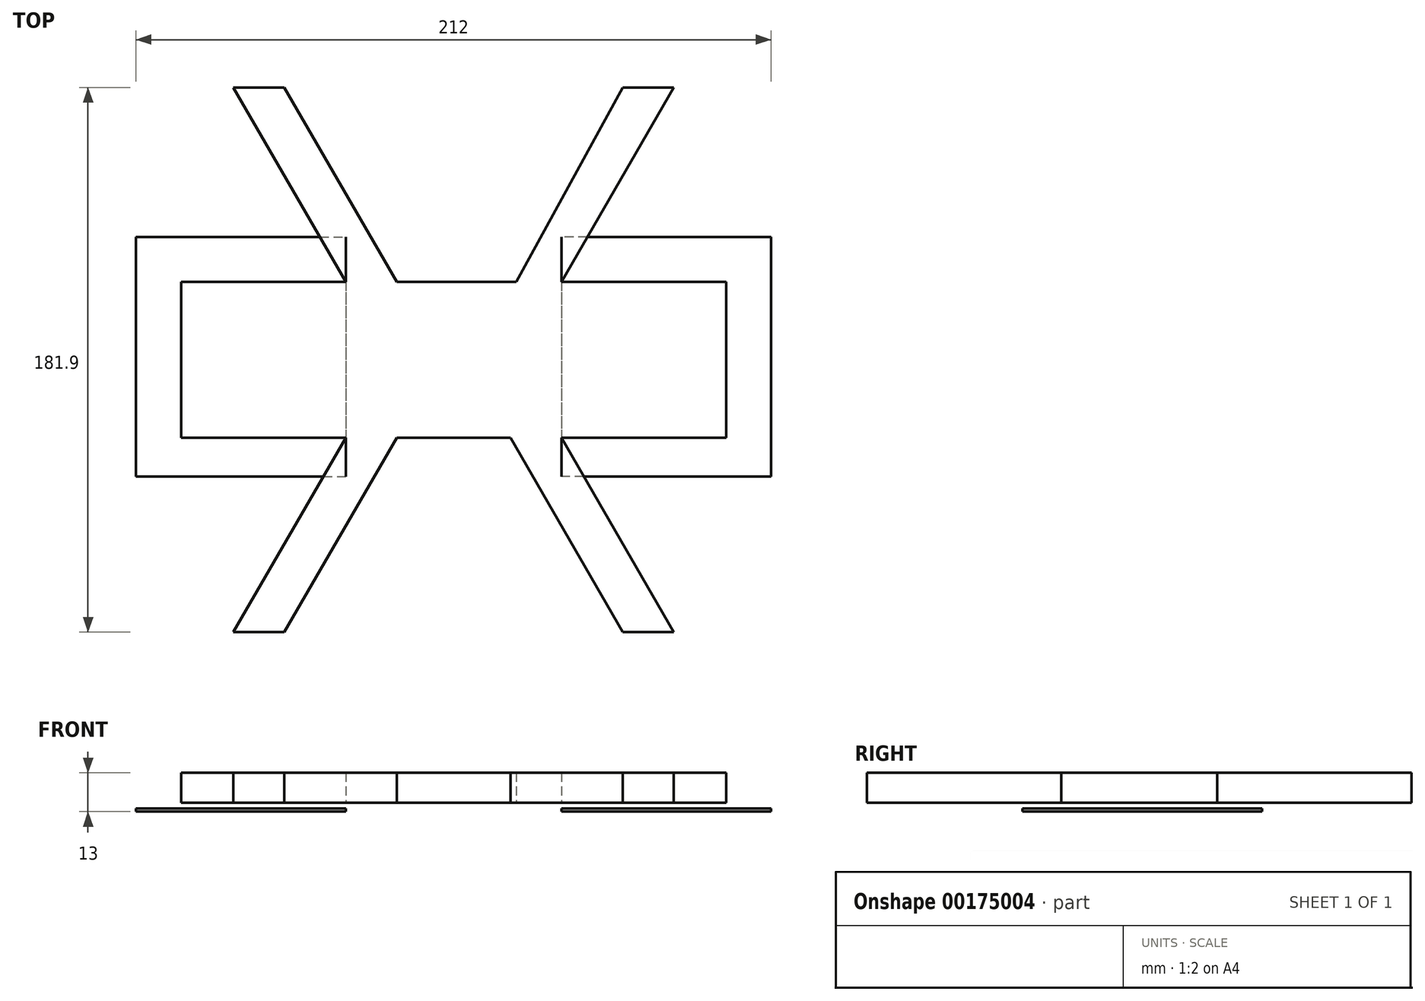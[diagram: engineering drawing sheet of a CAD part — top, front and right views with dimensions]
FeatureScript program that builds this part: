
annotation { "Feature Type Name" : "Feature", "Feature Type Description" : "" }
export const myFeature = defineFeature(function(context is Context, id is Id, definition is map)
    precondition{}
    {
        {
            var Q0;
            Q0=qCreatedBy(makeId("Top.planeOp"),FACE);
            var sketch = newSketch(context, id + "F0", { "sketchPlane" : qUnion([Q0])});
            skLineSegment(sketch, "E0.bottom", {"start": v(0, 0) * mm, "end": v(182, 0) * mm});
            skLineSegment(sketch, "E0.top", {"start": v(0, -52) * mm, "end": v(182, -52) * mm});
            skLineSegment(sketch, "E0.left", {"start": v(0, 0) * mm, "end": v(0, -52) * mm});
            skLineSegment(sketch, "E0.right", {"start": v(182, 0) * mm, "end": v(182, -52) * mm});
            skLineSegment(sketch, "E1", {"start": v(55, 0) * mm, "end": v(17.5, 64.95) * mm});
            skLineSegment(sketch, "E2", {"start": v(17.5, 64.95) * mm, "end": v(34.5, 64.95) * mm});
            skLineSegment(sketch, "E3", {"start": v(34.5, 64.95) * mm, "end": v(72, 0) * mm});
            skLineSegment(sketch, "E4", {"start": v(72, 0) * mm, "end": v(55, 0) * mm});
            skLineSegment(sketch, "E5", {"start": v(112, 0) * mm, "end": v(147.5, 64.95) * mm});
            skLineSegment(sketch, "E6", {"start": v(147.5, 64.95) * mm, "end": v(164.5, 64.95) * mm});
            skLineSegment(sketch, "E7", {"start": v(164.5, 64.95) * mm, "end": v(127, 0) * mm});
            skLineSegment(sketch, "E8", {"start": v(127, 0) * mm, "end": v(112, 0) * mm});
            skLineSegment(sketch, "E9", {"start": v(55, -52) * mm, "end": v(17.5, -116.95) * mm});
            skLineSegment(sketch, "E10", {"start": v(17.5, -116.95) * mm, "end": v(34.5, -116.95) * mm});
            skLineSegment(sketch, "E11", {"start": v(34.5, -116.95) * mm, "end": v(72, -52) * mm});
            skLineSegment(sketch, "E12", {"start": v(72, -52) * mm, "end": v(55, -52) * mm});
            skLineSegment(sketch, "E13", {"start": v(127, -52) * mm, "end": v(164.5, -116.95) * mm});
            skLineSegment(sketch, "E14", {"start": v(164.5, -116.95) * mm, "end": v(147.5, -116.95) * mm});
            skLineSegment(sketch, "E15", {"start": v(147.5, -116.95) * mm, "end": v(110, -52) * mm});
            skLineSegment(sketch, "E16", {"start": v(110, -52) * mm, "end": v(127, -52) * mm});
            skLineSegment(sketch, "E17", {"start": v(55, -52) * mm, "end": v(72, -52) * mm});
            skSolve(sketch);
        }
        {
            var Q0;
            Q0 = qSketchRegion(id + "F0", true);
            extrude(context, id + "F1", {"entities" : qUnion([Q0]), "depth" : 10 * mm});
        }
        {
            var Q0;
            Q0=qCreatedBy(makeId("Top.planeOp"),FACE);
            var sketch = newSketch(context, id + "F2", { "sketchPlane" : qUnion([Q0])});
            skLineSegment(sketch, "E18.bottom", {"start": v(-15, 15) * mm, "end": v(55, 15) * mm});
            skLineSegment(sketch, "E18.top", {"start": v(-15, -65) * mm, "end": v(55, -65) * mm});
            skLineSegment(sketch, "E18.left", {"start": v(-15, 15) * mm, "end": v(-15, -65) * mm});
            skLineSegment(sketch, "E18.right", {"start": v(55, 15) * mm, "end": v(55, -65) * mm});
            skLineSegment(sketch, "E19.bottom", {"start": v(197, 15) * mm, "end": v(127, 15) * mm});
            skLineSegment(sketch, "E19.top", {"start": v(197, -65) * mm, "end": v(127, -65) * mm});
            skLineSegment(sketch, "E19.left", {"start": v(197, 15) * mm, "end": v(197, -65) * mm});
            skLineSegment(sketch, "E19.right", {"start": v(127, 15) * mm, "end": v(127, -65) * mm});
            skSolve(sketch);
        }
        {
            var Q0;
            Q0 = qSketchRegion(id + "F2", true);
            extrude(context, id + "F3", {"entities" : qUnion([Q0]), "oppositeDirection" : true, "depth" : 3 * mm, "hasSecondDirection" : true, "secondDirectionOppositeDirection" : true, "secondDirectionDepth" : 2 * mm});
        }
    });
